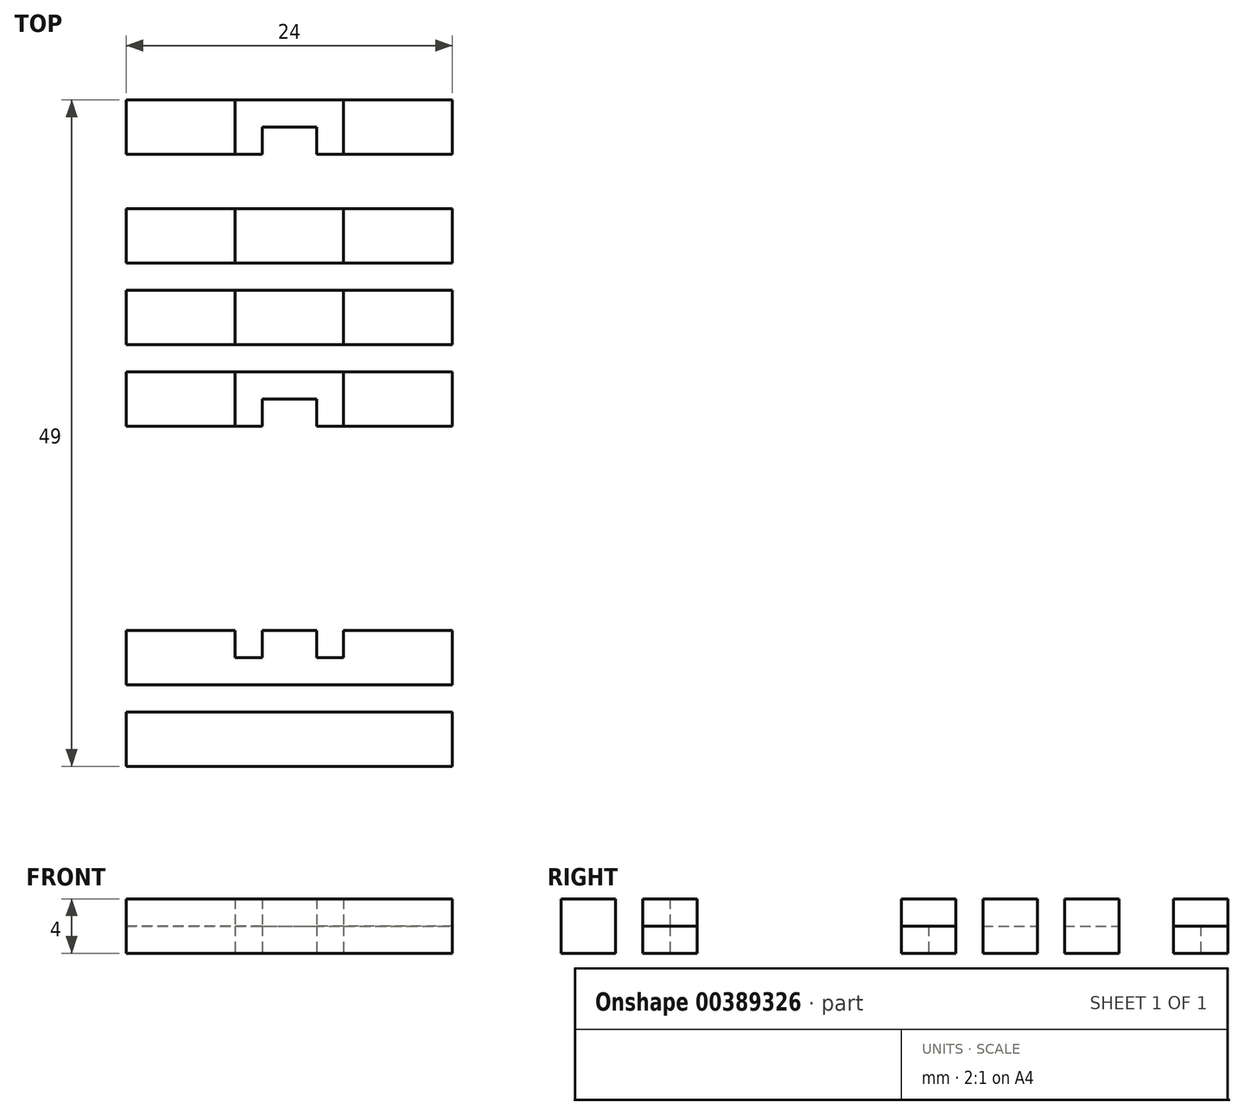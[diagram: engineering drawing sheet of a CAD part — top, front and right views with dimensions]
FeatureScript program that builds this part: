
annotation { "Feature Type Name" : "Feature", "Feature Type Description" : "" }
export const myFeature = defineFeature(function(context is Context, id is Id, definition is map)
    precondition{}
    {
        {
            assignVariable(context, id + "F0", {"name" : "WT", "anyValue" : 4});
        }
        {
            var Q0;
            Q0=qCreatedBy(makeId("Top.planeOp"),FACE);
            var sketch = newSketch(context, id + "F1", { "sketchPlane" : qUnion([Q0])});
            skLineSegment(sketch, "E0.bottom", {"start": v(-12, 2) * mm, "end": v(12, 2) * mm});
            skLineSegment(sketch, "E0.top", {"start": v(-12, -2) * mm, "end": v(12, -2) * mm});
            skLineSegment(sketch, "E0.left", {"start": v(-12, 2) * mm, "end": v(-12, -2) * mm});
            skLineSegment(sketch, "E0.right", {"start": v(12, 2) * mm, "end": v(12, -2) * mm});
            skPoint(sketch, "E0.middle", {"position": v(0, 0) * mm});
            skLineSegment(sketch, "E1", {"start": v(-4, 2) * mm, "end": v(-4, -2) * mm});
            skLineSegment(sketch, "E2", {"start": v(4, 2) * mm, "end": v(4, -2) * mm});
            skLineSegment(sketch, "E3", {"start": v(-12, -4) * mm, "end": v(12, -4) * mm});
            skLineSegment(sketch, "E4", {"start": v(12, -4) * mm, "end": v(12, -8) * mm});
            skLineSegment(sketch, "E5", {"start": v(12, -8) * mm, "end": v(-12, -8) * mm});
            skLineSegment(sketch, "E6", {"start": v(-12, -8) * mm, "end": v(-12, -4) * mm});
            skLineSegment(sketch, "E7", {"start": v(-2, -4) * mm, "end": v(-2, -8) * mm});
            skLineSegment(sketch, "E8", {"start": v(2, -8) * mm, "end": v(2, -4) * mm});
            skLineSegment(sketch, "E9", {"start": v(-2, -6) * mm, "end": v(2, -6) * mm});
            skLineSegment(sketch, "E10", {"start": v(-12, -23) * mm, "end": v(12, -23) * mm});
            skLineSegment(sketch, "E11", {"start": v(12, -23) * mm, "end": v(12, -27) * mm});
            skLineSegment(sketch, "E12", {"start": v(12, -27) * mm, "end": v(-12, -27) * mm});
            skLineSegment(sketch, "E13", {"start": v(-12, -27) * mm, "end": v(-12, -23) * mm});
            skLineSegment(sketch, "E14", {"start": v(-4, -23) * mm, "end": v(-4, -27) * mm});
            skLineSegment(sketch, "E15", {"start": v(4, -23) * mm, "end": v(4, -27) * mm});
            skLineSegment(sketch, "E16", {"start": v(-2, -27) * mm, "end": v(-2, -23) * mm});
            skLineSegment(sketch, "E17", {"start": v(2, -23) * mm, "end": v(2, -27) * mm});
            skLineSegment(sketch, "E18", {"start": v(-4, -25) * mm, "end": v(-2, -25) * mm});
            skLineSegment(sketch, "E19", {"start": v(4, -25) * mm, "end": v(2, -25) * mm});
            skLineSegment(sketch, "E20", {"start": v(-12, -29) * mm, "end": v(12, -29) * mm});
            skLineSegment(sketch, "E21", {"start": v(12, -29) * mm, "end": v(12, -33) * mm});
            skLineSegment(sketch, "E22", {"start": v(12, -33) * mm, "end": v(-12, -33) * mm});
            skLineSegment(sketch, "E23", {"start": v(-12, -33) * mm, "end": v(-12, -29) * mm});
            skSolve(sketch);
        }
        {
            var Q0;
            {var subQ0=sQuery(id+"F1.wireOp",EDGE,"E0.left");Q0=makeQuery(id+"F1.imprint","IMPRINT",FACE,{"disambiguationData":[TD([[makeQuery(id+"F1.imprint","IMPRINT",EDGE,{"derivedFrom":subQ0}),1.0]])]});}
            var Q1;
            {var subQ0=sQuery(id+"F1.wireOp",EDGE,"E1");Q1=makeQuery(id+"F1.imprint","IMPRINT",FACE,{"disambiguationData":[TD([[makeQuery(id+"F1.imprint","IMPRINT",EDGE,{"derivedFrom":subQ0}),1.0]])]});}
            var Q2;
            {var subQ0=sQuery(id+"F1.wireOp",EDGE,"E0.right");Q2=makeQuery(id+"F1.imprint","IMPRINT",FACE,{"disambiguationData":[TD([[makeQuery(id+"F1.imprint","IMPRINT",EDGE,{"derivedFrom":subQ0}),-1.0]])]});}
            extrude(context, id + "F2", {"entities" : qUnion([Q0, Q1, Q2]), "depth" : (getVariable(context, 'WT') / 2) * mm});
        }
        {
            var Q0;
            {var subQ0=sQuery(id+"F1.wireOp",EDGE,"E0.left");Q0=makeQuery(id+"F1.imprint","IMPRINT",FACE,{"disambiguationData":[TD([[makeQuery(id+"F1.imprint","IMPRINT",EDGE,{"derivedFrom":subQ0}),1.0]])]});}
            var Q1;
            {var subQ0=sQuery(id+"F1.wireOp",EDGE,"E0.right");Q1=makeQuery(id+"F1.imprint","IMPRINT",FACE,{"disambiguationData":[TD([[makeQuery(id+"F1.imprint","IMPRINT",EDGE,{"derivedFrom":subQ0}),-1.0]])]});}
            extrude(context, id + "F3", {"entities" : qUnion([Q0, Q1]), "operationType" : NewBodyOperationType.ADD, "depth" : (getVariable(context, 'WT')) * mm});
        }
        {
            var Q0;
            {var subQ4=sQuery(id+"F1.wireOp",EDGE,"E6");Q0=makeQuery(id+"F1.imprint","IMPRINT",FACE,{"disambiguationData":[TD([[makeQuery(id+"F1.imprint","IMPRINT",EDGE,{"derivedFrom":subQ4}),-1.0]])]});}
            var Q1;
            {var subQ5=sQuery(id+"F1.wireOp",EDGE,"E9");Q1=makeQuery(id+"F1.imprint","IMPRINT",FACE,{"disambiguationData":[TD([[makeQuery(id+"F1.imprint","IMPRINT",EDGE,{"derivedFrom":subQ5}),1.0]])]});}
            var Q2;
            {var subQ4=sQuery(id+"F1.wireOp",EDGE,"E4");Q2=makeQuery(id+"F1.imprint","IMPRINT",FACE,{"disambiguationData":[TD([[makeQuery(id+"F1.imprint","IMPRINT",EDGE,{"derivedFrom":subQ4}),-1.0]])]});}
            extrude(context, id + "F4", {"entities" : qUnion([Q0, Q1, Q2]), "depth" : (getVariable(context, 'WT')) / 2 * mm});
        }
        {
            var Q0;
            Q0=makeQuery(id+"F4.opExtrude","CAP_FACE",FACE,{"disambiguationData":[OSD([sQuery(id+"F1.wireOp",EDGE,"E3"),sQuery(id+"F1.wireOp",EDGE,"E4"),sQuery(id+"F1.wireOp",EDGE,"E5"),sQuery(id+"F1.wireOp",EDGE,"E6"),sQuery(id+"F1.wireOp",EDGE,"E7"),sQuery(id+"F1.wireOp",EDGE,"E8"),sQuery(id+"F1.wireOp",EDGE,"E9")])],"isStart":false});
            var sketch = newSketch(context, id + "F5", { "sketchPlane" : qUnion([Q0])});
            skLineSegment(sketch, "E24.0", {"start": v(-4, 2) * mm, "end": v(-4, -2) * mm, "construction": true});
            skLineSegment(sketch, "E25.0", {"start": v(4, -2) * mm, "end": v(4, 2) * mm, "construction": true});
            skLineSegment(sketch, "E26", {"start": v(-4, -4) * mm, "end": v(-4, -8) * mm});
            skLineSegment(sketch, "E27", {"start": v(4, -4) * mm, "end": v(4, -8) * mm});
            skLineSegment(sketch, "E28.0", {"start": v(-12, -4) * mm, "end": v(12, -4) * mm});
            skLineSegment(sketch, "E29.0", {"start": v(12, -4) * mm, "end": v(12, -8) * mm});
            skLineSegment(sketch, "E30.0", {"start": v(-12, -8) * mm, "end": v(-12, -4) * mm});
            skLineSegment(sketch, "E31.0", {"start": v(-2, -8) * mm, "end": v(-12, -8) * mm});
            skLineSegment(sketch, "E32.0", {"start": v(12, -8) * mm, "end": v(2, -8) * mm});
            skSolve(sketch);
        }
        {
            var Q0;
            {var subQ0=sQuery(id+"F5.wireOp",EDGE,"E26");Q0=makeQuery(id+"F5.imprint","IMPRINT",FACE,{"disambiguationData":[TD([[makeQuery(id+"F5.imprint","IMPRINT",EDGE,{"derivedFrom":subQ0}),-1.0]])]});}
            var Q1;
            {var subQ0=sQuery(id+"F5.wireOp",EDGE,"E27");Q1=makeQuery(id+"F5.imprint","IMPRINT",FACE,{"disambiguationData":[TD([[makeQuery(id+"F5.imprint","IMPRINT",EDGE,{"derivedFrom":subQ0}),1.0]])]});}
            extrude(context, id + "F6", {"entities" : qUnion([Q0, Q1]), "depth" : (getVariable(context, 'WT')) / 2 * mm});
        }
        {
            var Q0;
            {var subQ5=sQuery(id+"F1.wireOp",EDGE,"E18");Q0=makeQuery(id+"F1.imprint","IMPRINT",FACE,{"disambiguationData":[TD([[makeQuery(id+"F1.imprint","IMPRINT",EDGE,{"derivedFrom":subQ5}),-1.0]])]});}
            var Q1;
            {var subQ0=sQuery(id+"F1.wireOp",EDGE,"E16");var subQ7=sQuery(id+"F1.wireOp",EDGE,"E10");var subQ8=makeQuery(id+"F1.imprint","INTERSECT",VERTEX,{"derivedFrom":[subQ7,subQ0]});Q1=makeQuery(id+"F1.imprint","IMPRINT",FACE,{"disambiguationData":[TD([[makeQuery(id+"F1.imprint","IMPRINT",EDGE,{"disambiguationData":[TD([[subQ8,-1.0]])],"derivedFrom":subQ7}),-1.0]])]});}
            var Q2;
            {var subQ5=sQuery(id+"F1.wireOp",EDGE,"E19");Q2=makeQuery(id+"F1.imprint","IMPRINT",FACE,{"disambiguationData":[TD([[makeQuery(id+"F1.imprint","IMPRINT",EDGE,{"derivedFrom":subQ5}),1.0]])]});}
            var Q3;
            {var subQ1=sQuery(id+"F1.wireOp",EDGE,"E11");Q3=makeQuery(id+"F1.imprint","IMPRINT",FACE,{"disambiguationData":[TD([[makeQuery(id+"F1.imprint","IMPRINT",EDGE,{"derivedFrom":subQ1}),-1.0]])]});}
            var Q4;
            {var subQ4=sQuery(id+"F1.wireOp",EDGE,"E13");Q4=makeQuery(id+"F1.imprint","IMPRINT",FACE,{"disambiguationData":[TD([[makeQuery(id+"F1.imprint","IMPRINT",EDGE,{"derivedFrom":subQ4}),-1.0]])]});}
            extrude(context, id + "F7", {"entities" : qUnion([Q0, Q1, Q2, Q3, Q4]), "depth" : (getVariable(context, 'WT') / 2) * mm});
        }
        {
            var Q0;
            Q0=makeQuery(id+"F7.opExtrude","CAP_FACE",FACE,{"disambiguationData":[OSD([sQuery(id+"F1.wireOp",EDGE,"E10"),sQuery(id+"F1.wireOp",EDGE,"E11"),sQuery(id+"F1.wireOp",EDGE,"E12"),sQuery(id+"F1.wireOp",EDGE,"E13"),sQuery(id+"F1.wireOp",EDGE,"E14"),sQuery(id+"F1.wireOp",EDGE,"E15"),sQuery(id+"F1.wireOp",EDGE,"E16"),sQuery(id+"F1.wireOp",EDGE,"E17"),sQuery(id+"F1.wireOp",EDGE,"E18"),sQuery(id+"F1.wireOp",EDGE,"E19")])],"isStart":false});
            extrude(context, id + "F8", {"entities" : qUnion([Q0]), "depth" : (getVariable(context, 'WT')) / 2 * mm});
        }
        {
            var Q0;
            Q0=makeQuery(id+"F1.imprint","IMPRINT",FACE,{"disambiguationData":[TD([[makeQuery(id+"F1.imprint","IMPRINT",EDGE,{"derivedFrom":sQuery(id+"F1.wireOp",EDGE,"E20")}),-1.0]])]});
            extrude(context, id + "F9", {"entities" : qUnion([Q0]), "depth" : (getVariable(context, 'WT')) * mm});
        }
        {
            var Q0;
            Q0=makeQuery(id+"F2.opExtrude","SWEPT_BODY",BODY,{"disambiguationData":[OSD([sQuery(id+"F1.wireOp",EDGE,"E0.bottom"),sQuery(id+"F1.wireOp",EDGE,"E0.top"),sQuery(id+"F1.wireOp",EDGE,"E0.left"),sQuery(id+"F1.wireOp",EDGE,"E0.right")])]});
            transform(context, id + "F10", {"entities" : qUnion([Q0]), "transformType" : TransformType.TRANSLATION_3D, "dx" : 0 * mm, "dy" : (1.5 * getVariable(context, 'WT')) * mm, "dz" : 0 * mm, "makeCopy" : true});
        }
        {
            var Q0;
            Q0=makeQuery(id+"F4.opExtrude","SWEPT_BODY",BODY,{"disambiguationData":[OSD([sQuery(id+"F1.wireOp",EDGE,"E3"),sQuery(id+"F1.wireOp",EDGE,"E4"),sQuery(id+"F1.wireOp",EDGE,"E5"),sQuery(id+"F1.wireOp",EDGE,"E6"),sQuery(id+"F1.wireOp",EDGE,"E7"),sQuery(id+"F1.wireOp",EDGE,"E8"),sQuery(id+"F1.wireOp",EDGE,"E9")])]});
            transform(context, id + "F11", {"entities" : qUnion([Q0]), "transformType" : TransformType.TRANSLATION_3D, "dx" : 0 * mm, "dy" : (5 * getVariable(context, 'WT')) * mm, "dz" : 0 * mm, "makeCopy" : true});
        }
        {
            var Q0;
            Q0=makeQuery(id+"F6.opExtrude","SWEPT_BODY",BODY,{"disambiguationData":[OSD([sQuery(id+"F5.wireOp",EDGE,"E27"),sQuery(id+"F5.wireOp",EDGE,"E28.0"),sQuery(id+"F5.wireOp",EDGE,"E29.0"),sQuery(id+"F5.wireOp",EDGE,"E32.0")])]});
            transform(context, id + "F12", {"entities" : qUnion([Q0]), "transformType" : TransformType.TRANSLATION_3D, "dx" : 0 * mm, "dy" : (5 * getVariable(context, 'WT')) * mm, "dz" : 0 * mm, "makeCopy" : true});
        }
        {
            var Q0;
            Q0=makeQuery(id+"F6.opExtrude","SWEPT_BODY",BODY,{"disambiguationData":[OSD([sQuery(id+"F5.wireOp",EDGE,"E26"),sQuery(id+"F5.wireOp",EDGE,"E28.0"),sQuery(id+"F5.wireOp",EDGE,"E30.0"),sQuery(id+"F5.wireOp",EDGE,"E31.0")])]});
            transform(context, id + "F13", {"entities" : qUnion([Q0]), "transformType" : TransformType.TRANSLATION_3D, "dx" : 0 * mm, "dy" : 5 * getVariable(context, 'WT') * mm, "dz" : 0 * mm, "makeCopy" : true});
        }
    });
